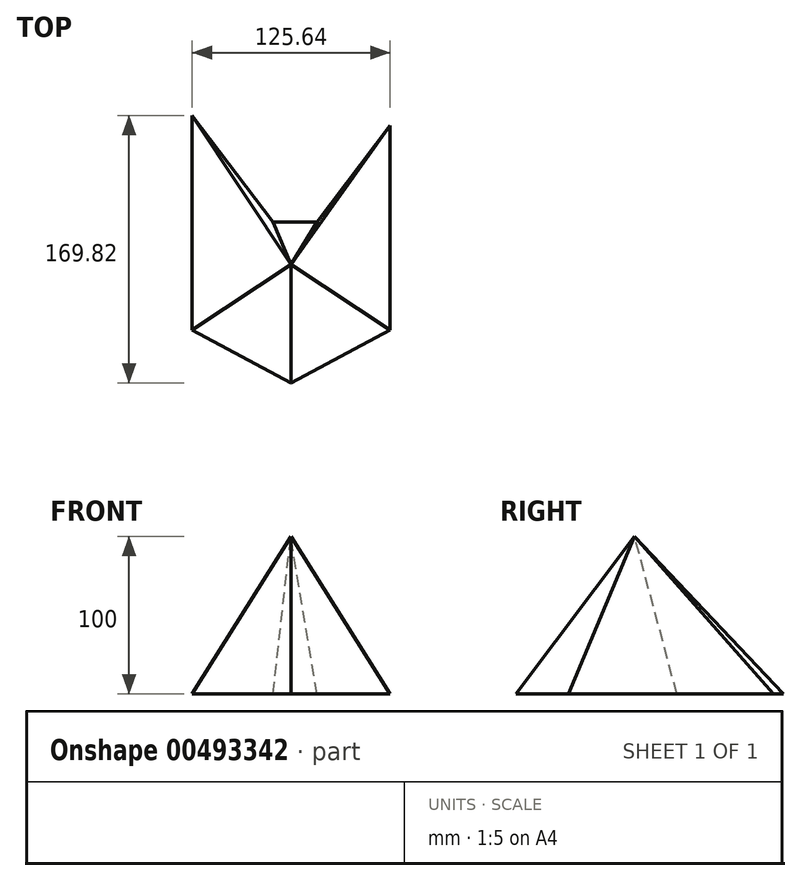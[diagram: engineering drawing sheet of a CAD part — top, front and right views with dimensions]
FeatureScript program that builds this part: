
annotation { "Feature Type Name" : "Feature", "Feature Type Description" : "" }
export const myFeature = defineFeature(function(context is Context, id is Id, definition is map)
    precondition{}
    {
        {
            var Q0;
            Q0=qCreatedBy(makeId("Top.planeOp"),FACE);
            var sketch = newSketch(context, id + "F0", { "sketchPlane" : qUnion([Q0])});
            skLineSegment(sketch, "E0", {"start": v(-62.69, 20.04) * mm, "end": v(-62.69, -41.83) * mm});
            skLineSegment(sketch, "E1", {"start": v(-62.69, -41.83) * mm, "end": v(0, -75.33) * mm});
            skLineSegment(sketch, "E2", {"start": v(0, -75.33) * mm, "end": v(62.95, -41.83) * mm});
            skLineSegment(sketch, "E3", {"start": v(62.95, -41.83) * mm, "end": v(62.95, 16.27) * mm});
            skLineSegment(sketch, "E4", {"start": v(62.95, 16.27) * mm, "end": v(62.95, 88.19) * mm});
            skLineSegment(sketch, "E5", {"start": v(62.95, 88.19) * mm, "end": v(16.5, 26.91) * mm});
            skLineSegment(sketch, "E6", {"start": v(16.5, 26.91) * mm, "end": v(-11.3, 26.91) * mm});
            skLineSegment(sketch, "E7", {"start": v(-11.3, 26.91) * mm, "end": v(-62.69, 94.5) * mm});
            skLineSegment(sketch, "E8", {"start": v(-62.69, 94.5) * mm, "end": v(-62.69, 20.04) * mm});
            skSolve(sketch);
        }
        {
            var Q0;
            Q0=qCreatedBy(makeId("Top.planeOp"),FACE);
            cPlane(context, id + "F1", {"entities" : qUnion([Q0]), "cplaneType" : CPlaneType.OFFSET, "offset" : 100 * mm, "width" : 150 * mm, "height" : 150 * mm});
        }
        {
            var Q0;
            Q0=qCreatedBy(id+"F1.planeOp",FACE);
            var sketch = newSketch(context, id + "F2", { "sketchPlane" : qUnion([Q0])});
            skPoint(sketch, "E9", {"position": v(0, 0) * mm});
            skSolve(sketch);
        }
        {
            var Q0;
            Q0=makeQuery(id+"F0.imprint","IMPRINT",FACE,{"disambiguationData":[TD([[makeQuery(id+"F0.imprint","IMPRINT",EDGE,{"derivedFrom":sQuery(id+"F0.wireOp",EDGE,"E0")}),1.0]])]});
            var Q1;
            Q1=sQuery(id+"F2.wireOp",VERTEX,"E9");
            loft(context, id + "F3", {"sheetProfilesArray" : [{ "sheetProfileEntities" : qUnion([Q0]) }, { "sheetProfileEntities" : qUnion([Q1]) }]});
        }
    });
